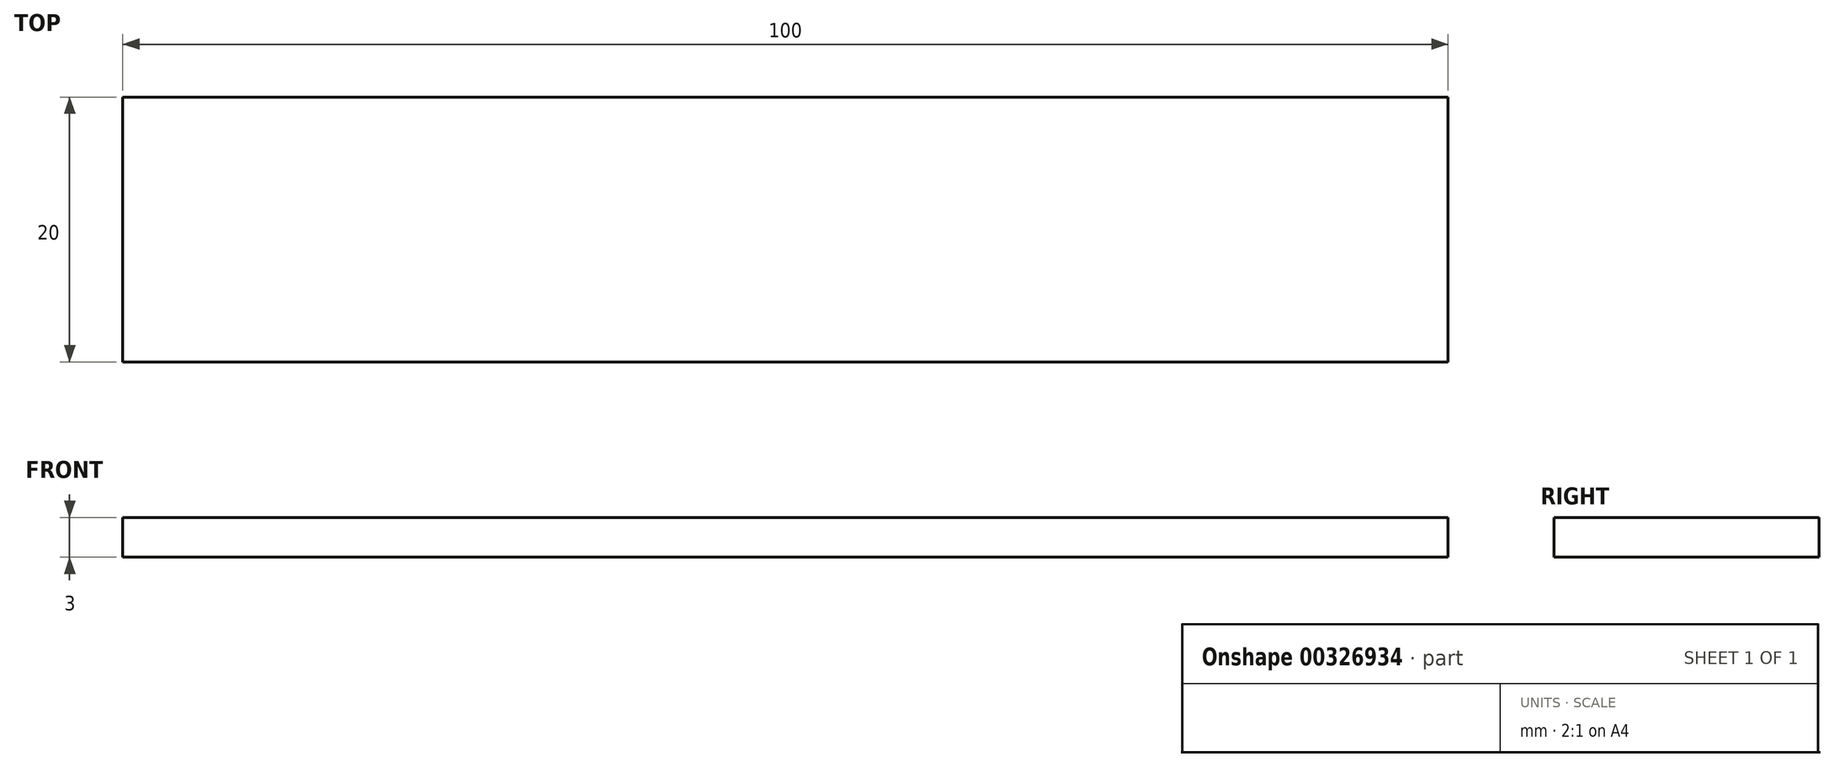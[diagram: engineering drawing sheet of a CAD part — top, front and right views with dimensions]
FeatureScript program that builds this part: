
annotation { "Feature Type Name" : "Feature", "Feature Type Description" : "" }
export const myFeature = defineFeature(function(context is Context, id is Id, definition is map)
    precondition{}
    {
        {
            var Q0;
            Q0=qCreatedBy(makeId("Top.planeOp"),FACE);
            var sketch = newSketch(context, id + "F0", { "sketchPlane" : qUnion([Q0])});
            skLineSegment(sketch, "E0.bottom", {"start": v(0, 0) * mm, "end": v(100, 0) * mm});
            skLineSegment(sketch, "E0.top", {"start": v(0, 20) * mm, "end": v(100, 20) * mm});
            skLineSegment(sketch, "E0.left", {"start": v(0, 0) * mm, "end": v(0, 20) * mm});
            skLineSegment(sketch, "E0.right", {"start": v(100, 0) * mm, "end": v(100, 20) * mm});
            skSolve(sketch);
        }
        {
            var Q0;
            Q0 = qSketchRegion(id + "F0", true);
            extrude(context, id + "F1", {"entities" : qUnion([Q0]), "depth" : 3 * mm});
        }
    });
